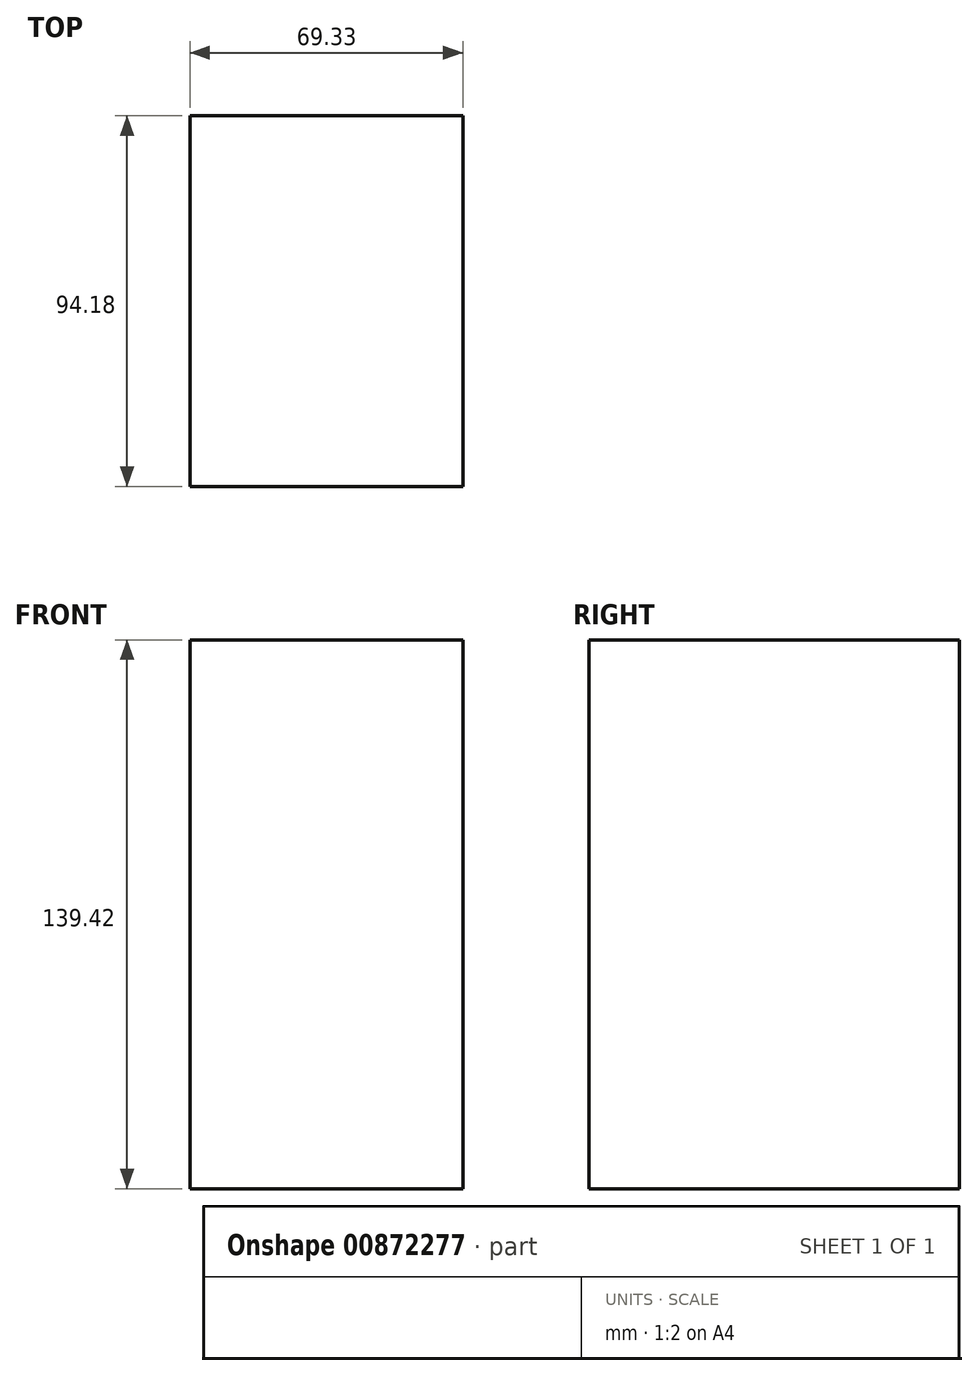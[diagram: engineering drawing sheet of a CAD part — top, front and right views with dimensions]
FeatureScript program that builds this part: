
annotation { "Feature Type Name" : "Feature", "Feature Type Description" : "" }
export const myFeature = defineFeature(function(context is Context, id is Id, definition is map)
    precondition{}
    {
        {
            var Q0;
            Q0=qCreatedBy(makeId("Top.planeOp"),FACE);
            var sketch = newSketch(context, id + "F0", { "sketchPlane" : qUnion([Q0])});
            skLineSegment(sketch, "E0.bottom", {"start": v(-26.68, -51.14) * mm, "end": v(42.65, -51.14) * mm});
            skLineSegment(sketch, "E0.top", {"start": v(-26.68, 43.04) * mm, "end": v(42.65, 43.04) * mm});
            skLineSegment(sketch, "E0.left", {"start": v(-26.68, -51.14) * mm, "end": v(-26.68, 43.04) * mm});
            skLineSegment(sketch, "E0.right", {"start": v(42.65, -51.14) * mm, "end": v(42.65, 43.04) * mm});
            skSolve(sketch);
        }
        {
            var Q0;
            Q0=makeQuery(id+"F0.imprint","IMPRINT",FACE,{"disambiguationData":[TD([[makeQuery(id+"F0.imprint","IMPRINT",EDGE,{"derivedFrom":sQuery(id+"F0.wireOp",EDGE,"E0.bottom")}),1.0]])]});
            var sketch = newSketch(context, id + "F1", { "sketchPlane" : qUnion([Q0])});
            skSolve(sketch);
        }
        {
            var Q0;
            Q0=makeQuery(id+"F1.imprint","IMPRINT",FACE,{"disambiguationData":[TD([[makeQuery(id+"F1.imprint","IMPRINT",EDGE,{"derivedFrom":makeQuery(id+"F0.imprint","IMPRINT",EDGE,{"derivedFrom":sQuery(id+"F0.wireOp",EDGE,"E0.bottom")})}),1.0]])]});
            extrude(context, id + "F2", {"entities" : qUnion([Q0]), "depth" : 139.42 * mm, "offsetDistance" : 25 * mm});
        }
    });
